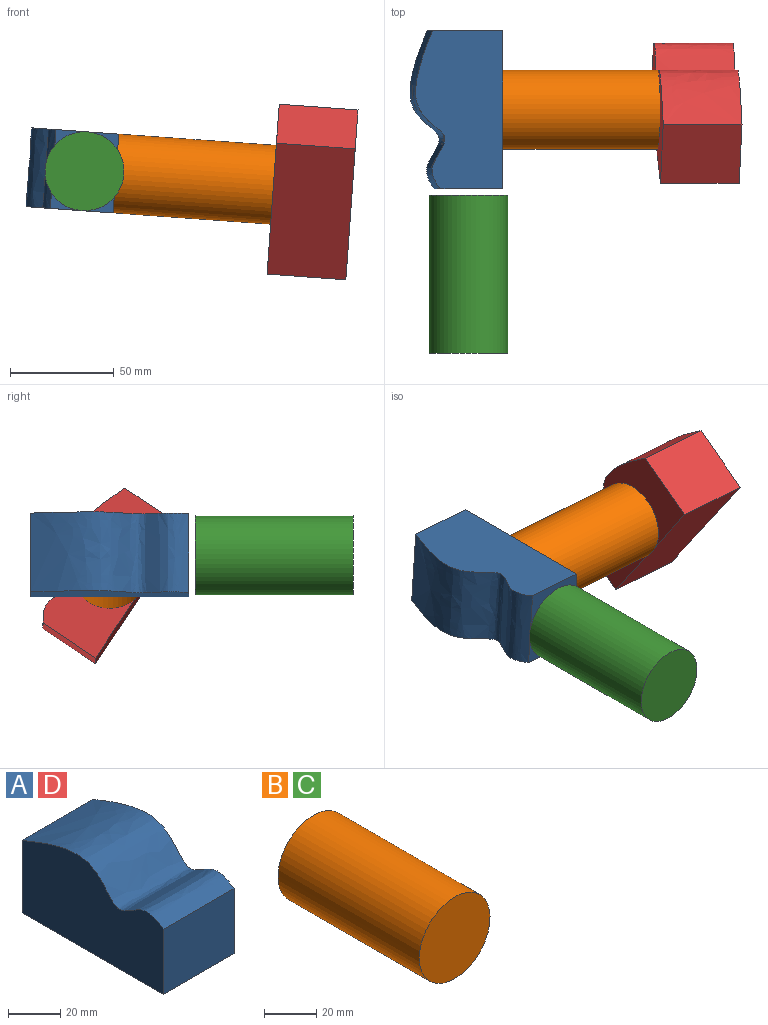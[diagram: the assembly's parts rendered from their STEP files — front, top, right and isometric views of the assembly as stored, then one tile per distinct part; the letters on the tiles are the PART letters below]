
ASSEMBLY  parts=4 mates=3
PART A: 6 faces, bbox 38.1x78.1x43.1 mm
  f0: plane 78.1x43.08mm, normal (-1,0,0), area 2743.7mm2, adj f2,f3,f4,f5
  f1: plane 78.1x43.08mm, normal (1,0,0), area 2743.7mm2, adj f2,f3,f4,f5
  f2: plane 38.1x30.37mm, normal (0,-1,0), area 1157mm2, adj f0,f1,f4,f5
  f3: plane 38.1x33.88mm, normal (0,1,0), area 1290.8mm2, adj f0,f1,f4,f5
  f4: plane 76.2x38.1mm, normal (0,0,-1), area 2903.2mm2, adj f0,f1,f2,f3
  f5: extruded ~76.2x38.1mm, area 3235.4mm2, adj f0,f1,f2,f3
PART B: 3 faces, bbox 38.1x76.2x38.1 mm
  f0: cylinder r=19.05mm len=76.2mm, axis (0,1,0), area 9120.7mm2, adj f1,f2
  f1: plane 38.1x38.1mm, normal (0,-1,0), area 1140.1mm2, adj f0
  f2: plane 38.1x38.1mm, normal (0,1,0), area 1140.1mm2, adj f0
PART C: same geometry as B
PART D: same geometry as A
PLACE A rot(axis=(0,-1,0),85.9deg) t=(-41.69,53.02,-161.08)mm
PLACE B rot(axis=(-0.71,-0.69,-0.14),158deg) t=(25.72,14.92,-46.54)mm
PLACE C t=(-65.43,-26.35,-40.01)mm fixed
PLACE D rot(axis=(-0.03,-0.47,-0.88),178.1deg) t=(164.23,-34.8,-45.88)mm
MATE revolute D.f1 <-> B.f0  axis (-1,0,0.07) through (25.72,14.92,-46.54)mm
MATE revolute B.f0 <-> A.f4  axis (1,0,-0.07) through (-50.29,14.92,-41.09)mm
MATE revolute A.f2 <-> C.f0  axis (0,-1,0) through (-65.43,-23.18,-40.01)mm
